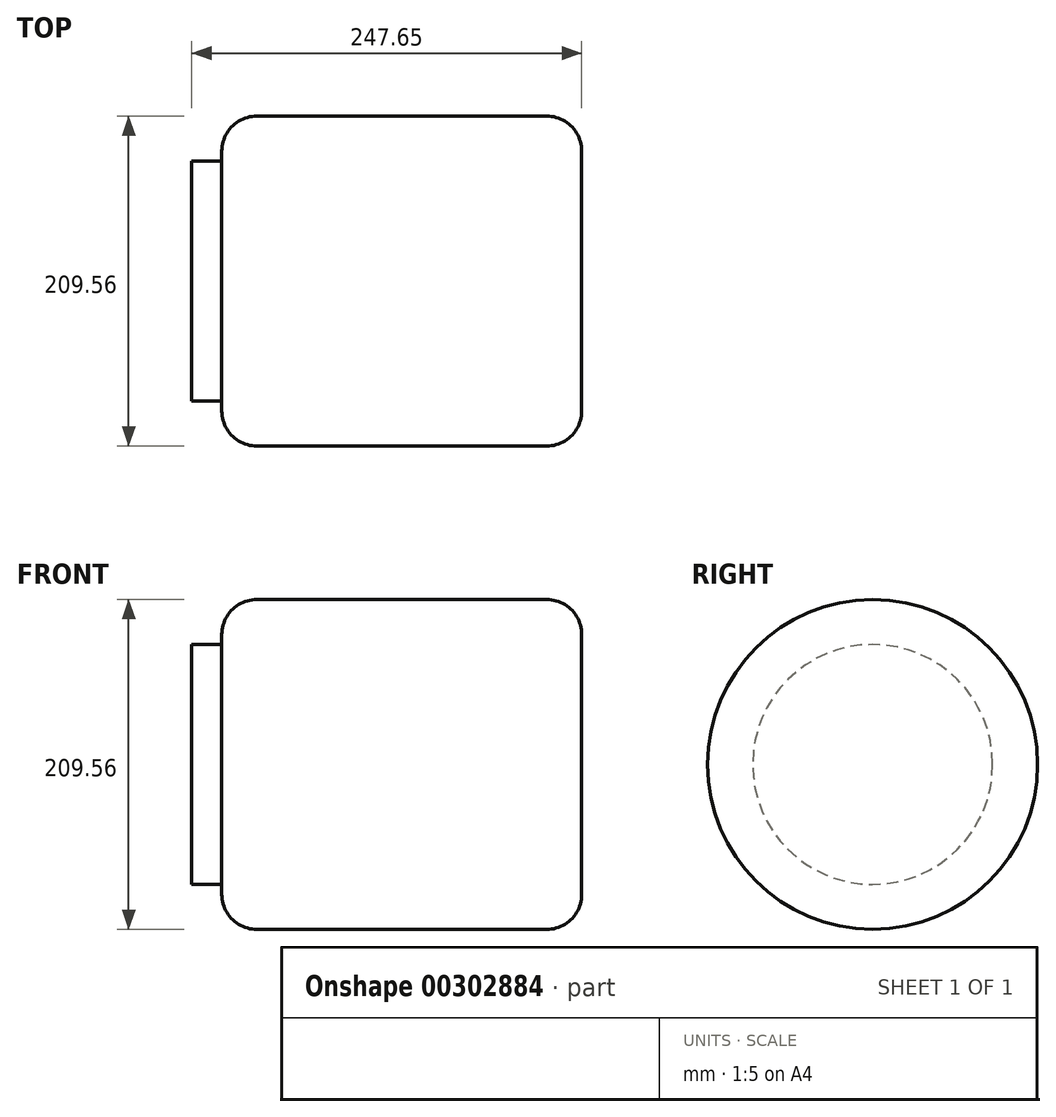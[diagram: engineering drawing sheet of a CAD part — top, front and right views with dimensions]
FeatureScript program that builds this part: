
annotation { "Feature Type Name" : "Feature", "Feature Type Description" : "" }
export const myFeature = defineFeature(function(context is Context, id is Id, definition is map)
    precondition{}
    {
        {
            var Q0;
            Q0=qCreatedBy(makeId("Right.planeOp"),FACE);
            var sketch = newSketch(context, id + "F0", { "sketchPlane" : qUnion([Q0])});
            skCircle(sketch, "E0", {"center": v(0, 0) * mm, "radius": 104.78 * mm});
            skSolve(sketch);
        }
        {
            var Q0;
            Q0 = qSketchRegion(id + "F0", true);
            extrude(context, id + "F1", {"entities" : qUnion([Q0]), "depth" : 114.3 * mm, "hasSecondDirection" : true, "secondDirectionOppositeDirection" : true, "secondDirectionDepth" : 114.3 * mm});
        }
        {
            var Q0;
            Q0=makeQuery(id+"F1.opExtrude","CAP_FACE",FACE,{"disambiguationData":[OSD([sQuery(id+"F0.wireOp",EDGE,"E0")])],"isStart":true});
            var sketch = newSketch(context, id + "F2", { "sketchPlane" : qUnion([Q0])});
            skCircle(sketch, "E1", {"center": v(0, 0) * mm, "radius": 76.2 * mm});
            skSolve(sketch);
        }
        {
            var Q0;
            Q0 = qSketchRegion(id + "F2", true);
            extrude(context, id + "F3", {"entities" : qUnion([Q0]), "operationType" : NewBodyOperationType.ADD, "depth" : 19.05 * mm});
        }
        {
            var Q0;
            Q0=makeQuery(id+"F1.opExtrude","CAP_EDGE",EDGE,{"disambiguationData":[OSD([sQuery(id+"F0.wireOp",EDGE,"E0")])],"isStart":true});
            var Q1;
            Q1=makeQuery(id+"F1.opExtrude","CAP_EDGE",EDGE,{"disambiguationData":[OSD([sQuery(id+"F0.wireOp",EDGE,"E0")])],"isStart":false});
            fillet(context, id + "F4", {"entities" : qUnion([Q0, Q1]), "radius" : 22.22 * mm, "tangentPropagation" : true, "allowEdgeOverflow" : false});
        }
    });
